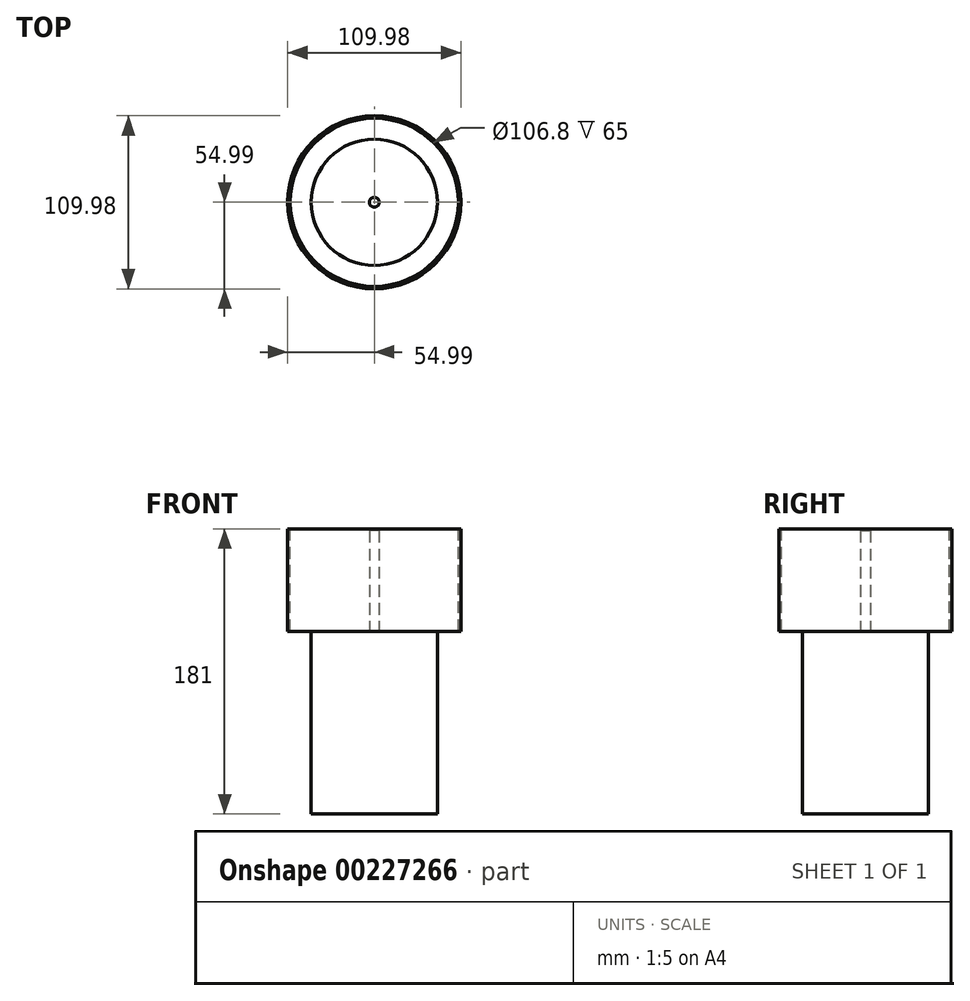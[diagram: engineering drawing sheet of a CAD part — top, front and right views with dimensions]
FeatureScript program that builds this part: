
annotation { "Feature Type Name" : "Feature", "Feature Type Description" : "" }
export const myFeature = defineFeature(function(context is Context, id is Id, definition is map)
    precondition{}
    {
        {
            var Q0;
            Q0=qCreatedBy(makeId("Top.planeOp"),FACE);
            var sketch = newSketch(context, id + "F0", { "sketchPlane" : qUnion([Q0])});
            skCircle(sketch, "E0", {"center": v(0, 0) * mm, "radius": 54.99 * mm});
            skSolve(sketch);
        }
        {
            var Q0;
            Q0 = qSketchRegion(id + "F0", true);
            extrude(context, id + "F1", {"entities" : qUnion([Q0]), "depth" : 65 * mm});
        }
        {
            var Q0;
            Q0=makeQuery(id+"F1.opExtrude","CAP_FACE",FACE,{"disambiguationData":[OSD([sQuery(id+"F0.wireOp",EDGE,"E0")])],"isStart":false});
            var sketch = newSketch(context, id + "F2", { "sketchPlane" : qUnion([Q0])});
            skCircle(sketch, "E1", {"center": v(0, 0) * mm, "radius": 53.4 * mm});
            skSolve(sketch);
        }
        {
            var Q0;
            Q0=sQuery(id+"F2.wireOp",VERTEX,"E1.center");
            var Q1;
            Q1=makeQuery(id+"F1.opExtrude","SWEPT_BODY",BODY,{"disambiguationData":[OSD([sQuery(id+"F0.wireOp",EDGE,"E0")])]});
            hole(context, id + "F3", {"style" : HoleStyle.SIMPLE, "endStyle" : HoleEndStyle.THROUGH, "holeDiameter" : 106.8 * mm, "locations" : qUnion([Q0]), "scope" : qUnion([Q1]), "isTappedThrough" : true});
        }
        {
            var Q0;
            Q0=qCreatedBy(makeId("Top.planeOp"),FACE);
            var sketch = newSketch(context, id + "F4", { "sketchPlane" : qUnion([Q0])});
            skCircle(sketch, "E2", {"center": v(0, 0) * mm, "radius": 3.12 * mm});
            skSolve(sketch);
        }
        {
            var Q0;
            Q0=makeQuery(id+"F4.imprint","IMPRINT",FACE,{"disambiguationData":[TD([[makeQuery(id+"F4.imprint","IMPRINT",EDGE,{"derivedFrom":sQuery(id+"F4.wireOp",EDGE,"E2")}),1.0]])]});
            extrude(context, id + "F5", {"entities" : qUnion([Q0]), "depth" : 63.9 * mm});
        }
        {
            var Q0;
            Q0=qCreatedBy(makeId("Top.planeOp"),FACE);
            var sketch = newSketch(context, id + "F6", { "sketchPlane" : qUnion([Q0])});
            skCircle(sketch, "E3", {"center": v(0, 0) * mm, "radius": 40.08 * mm});
            skSolve(sketch);
        }
        {
            var Q0;
            Q0 = qSketchRegion(id + "F6", true);
            extrude(context, id + "F7", {"entities" : qUnion([Q0]), "operationType" : NewBodyOperationType.ADD, "oppositeDirection" : true, "depth" : 116 * mm});
        }
    });
